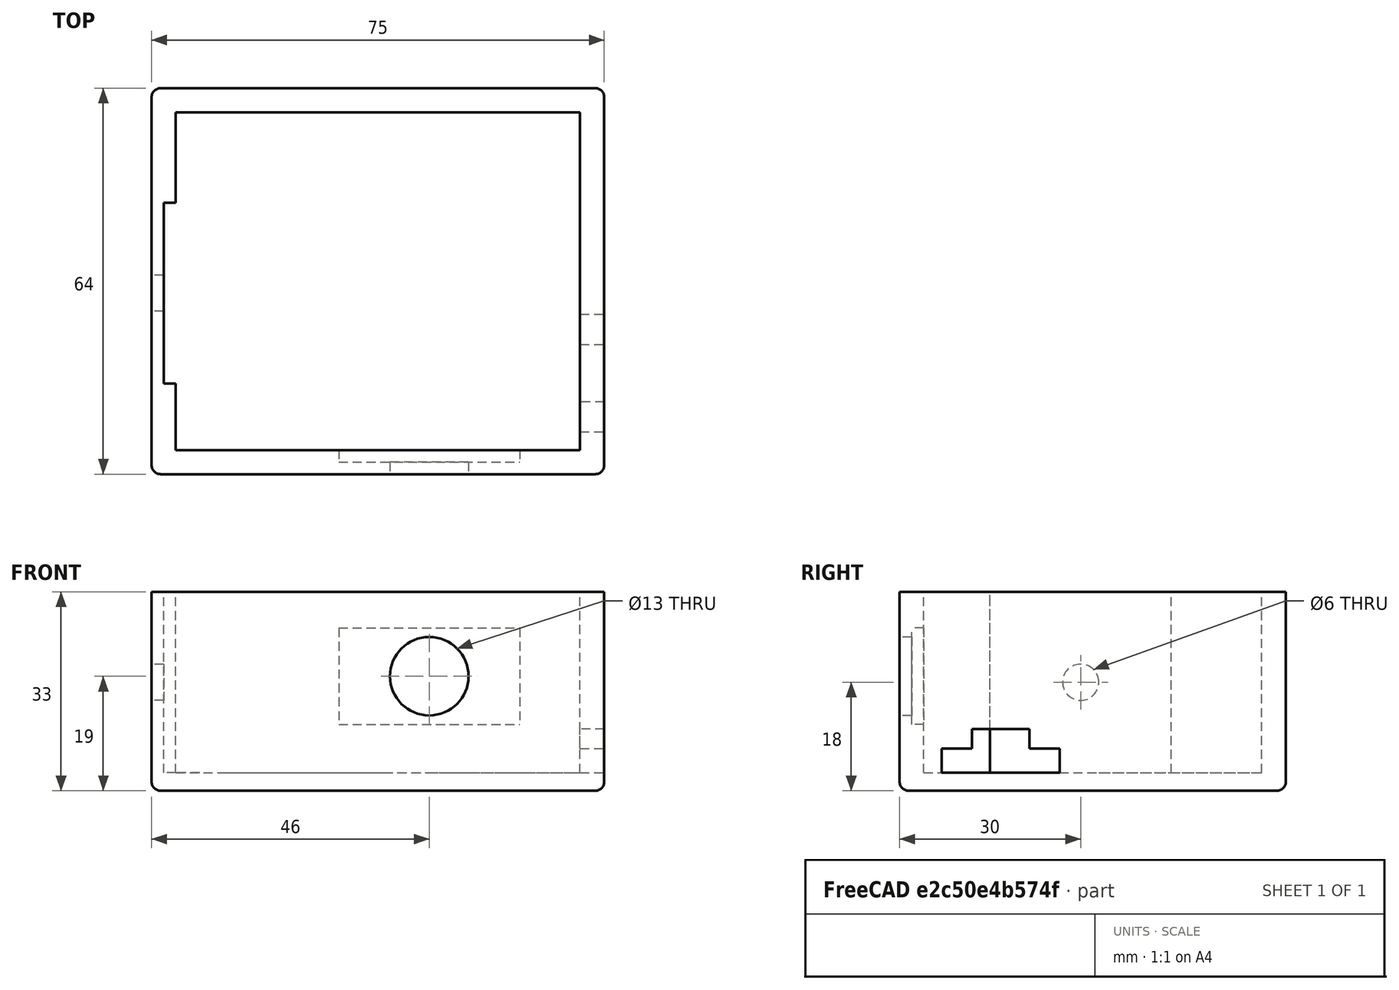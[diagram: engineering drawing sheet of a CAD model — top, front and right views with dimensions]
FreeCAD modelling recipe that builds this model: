
FCSTD DOCUMENT  (FreeCAD 0.19R)
Label: RoundTimer-box
License: All rights reserved
LicenseURL: http://en.wikipedia.org/wiki/All_rights_reserved
objects: Part::Box×14, Part::Cylinder×6, Part::MultiFuse×5, Part::Cut×5, Part::Fuse×2, Part::Fillet×1
note: 33 computed .brp shape members not serialized (recipe doc carries the construction recipe); baked Part::Feature solids carry a one-line shape summary decoded from their .brp

FEATURE [Part::Box] Box  label="Cube"
  AttacherType = Attacher::AttachEngine3D
  Height = 30
  Length = 30
  Width = 16
FEATURE [Part::Cylinder] Cylinder
  Angle = 360
  AttacherType = Attacher::AttachEngine3D
  Height = 9
  Placement = pos=(15,8,30) rot=(0,0,1;0rad)
  Radius = 6.5
FEATURE [Part::Fuse] Fusion  label="Awesome switch"
  Base = -> Box
  Placement = pos=(-11,17,8) rot=(1,0,0;1.5708rad)
  Tool = -> Cylinder
FEATURE [Part::Box] Box001  label="Cube001"
  AttacherType = Attacher::AttachEngine3D
  Height = 6
  Length = 51
  Width = 28
FEATURE [Part::Box] Box002  label="Cube002"
  AttacherType = Attacher::AttachEngine3D
  Height = 7
  Length = 51
  Placement = pos=(0,2,6) rot=(0,0,1;0rad)
  Width = 24
FEATURE [Part::MultiFuse] Fusion001  label="LCD Display"
  Placement = pos=(-5,-8,25) rot=(0,0,1;1.5708rad)
  Shapes = -> [Box001,Box002]
FEATURE [Part::Box] Box003  label="Lipo Battery"
  AttacherType = Attacher::AttachEngine3D
  Height = 12
  Length = 50
  Placement = pos=(-22,18,0) rot=(0,0,1;0rad)
  Width = 27
FEATURE [Part::Cylinder] Cylinder001
  Angle = 360
  AttacherType = Attacher::AttachEngine3D
  Height = 19
  Radius = 4.65
FEATURE [Part::Cylinder] Cylinder002
  Angle = 360
  AttacherType = Attacher::AttachEngine3D
  Height = 6.7
  Placement = pos=(0,0,19) rot=(0,0,1;0rad)
  Radius = 3.6
FEATURE [Part::MultiFuse] Fusion002  label="Push Button mode/reset"
  Placement = pos=(20,35,12) rot=(1,0,0;0rad)
  Shapes = -> [Cylinder001,Cylinder002]
FEATURE [Part::Cylinder] Cylinder003
  Angle = 360
  AttacherType = Attacher::AttachEngine3D
  Height = 19
  Radius = 4.65
FEATURE [Part::Cylinder] Cylinder004
  Angle = 360
  AttacherType = Attacher::AttachEngine3D
  Height = 6.7
  Placement = pos=(0,0,19) rot=(0,0,1;0rad)
  Radius = 3.6
FEATURE [Part::MultiFuse] Fusion003  label="Push Button start/stop"
  Placement = pos=(3,35,12) rot=(1,0,0;0rad)
  Shapes = -> [Cylinder003,Cylinder004]
FEATURE [Part::Box] Box004  label="Cube003"
  AttacherType = Attacher::AttachEngine3D
  Height = 7.25
  Length = 29
  Width = 19.5
FEATURE [Part::Box] Box005  label="Cube004"
  AttacherType = Attacher::AttachEngine3D
  Height = 4
  Length = 10
  Placement = pos=(28,5.75,1.75) rot=(0,0,1;0rad)
  Width = 8
FEATURE [Part::Box] Box006  label="Cube005"
  AttacherType = Attacher::AttachEngine3D
  Height = 10
  Length = 10
  Placement = pos=(19,-5,4) rot=(0,0,1;0rad)
  Width = 10
FEATURE [Part::MultiFuse] Fusion004
  Shapes = -> [Box004,Box005]
FEATURE [Part::Cut] Cut
  Base = -> Fusion004
  Tool = -> Box006
FEATURE [Part::Box] Box007  label="Cube006"
  AttacherType = Attacher::AttachEngine3D
  Height = 10
  Length = 10
  Placement = pos=(19,14.5,4) rot=(0,0,1;0rad)
  Width = 10
FEATURE [Part::Cut] Cut001  label="USB Battery Charger"
  Base = -> Cut
  Placement = pos=(4,-8,0) rot=(0,0,1;0rad)
  Tool = -> Box007
FEATURE [Part::Box] Box008  label="Piezo Driver"
  AttacherType = Attacher::AttachEngine3D
  Height = 12.2
  Length = 28
  Placement = pos=(-30,-7,0) rot=(0,0,1;0rad)
  Width = 18
FEATURE [Part::Box] Box009  label="Cube007"
  AttacherType = Attacher::AttachEngine3D
  Height = 6
  Length = 30
  Width = 30
FEATURE [Part::Cylinder] Cylinder005
  Angle = 360
  AttacherType = Attacher::AttachEngine3D
  Height = 10
  Placement = pos=(15,15,0) rot=(0,0,1;0rad)
  Radius = 3
FEATURE [Part::Fuse] Fusion005  label="Piezo Buzzer"
  Base = -> Box009
  Placement = pos=(-34,0,0) rot=(0,1,0;-1.5708rad)
  Tool = -> Cylinder005
FEATURE [Part::Box] Box010  label="OuterBox"
  AttacherType = Attacher::AttachEngine3D
  Height = 36
  Length = 75
  Placement = pos=(-42,-15,-3) rot=(0,0,1;0rad)
  Width = 64
FEATURE [Part::Box] Box011  label="InnerBox"
  AttacherType = Attacher::AttachEngine3D
  Height = 30
  Length = 67
  Placement = pos=(-38,-11,0) rot=(0,0,1;0rad)
  Width = 56
FEATURE [Part::Box] Box012  label="LidRemove"
  AttacherType = Attacher::AttachEngine3D
  Height = 4
  Length = 75
  Placement = pos=(-42,-15,30) rot=(0,0,1;0rad)
  Width = 64
FEATURE [Part::Box] Box013  label="Arduino"
  AttacherType = Attacher::AttachEngine3D
  Height = 3.5
  Length = 27
  Placement = pos=(-35,19,12) rot=(0,0,1;0rad)
  Width = 15.5
FEATURE [Part::Fillet] Fillet
  Base = -> Box010
  Edges = 12 edges r=1.5: [Edge1,Edge2,Edge3,Edge4,Edge5,Edge6,Edge7,Edge8,Edge9,Edge10,Edge11,Edge12]
FEATURE [Part::Cut] Cut002
  Base = -> Fillet
  Tool = -> Box011
FEATURE [Part::Cut] Cut003
  Base = -> Cut002
  Tool = -> Box012
FEATURE [Part::MultiFuse] Fusion006  label="parts"
  Shapes = -> [Box013,Fusion005,Box008,Cut001,Fusion003,Fusion002,Box003,Fusion001,Fusion]
FEATURE [Part::Cut] Cut004
  Base = -> Cut003
  Tool = -> Fusion006
